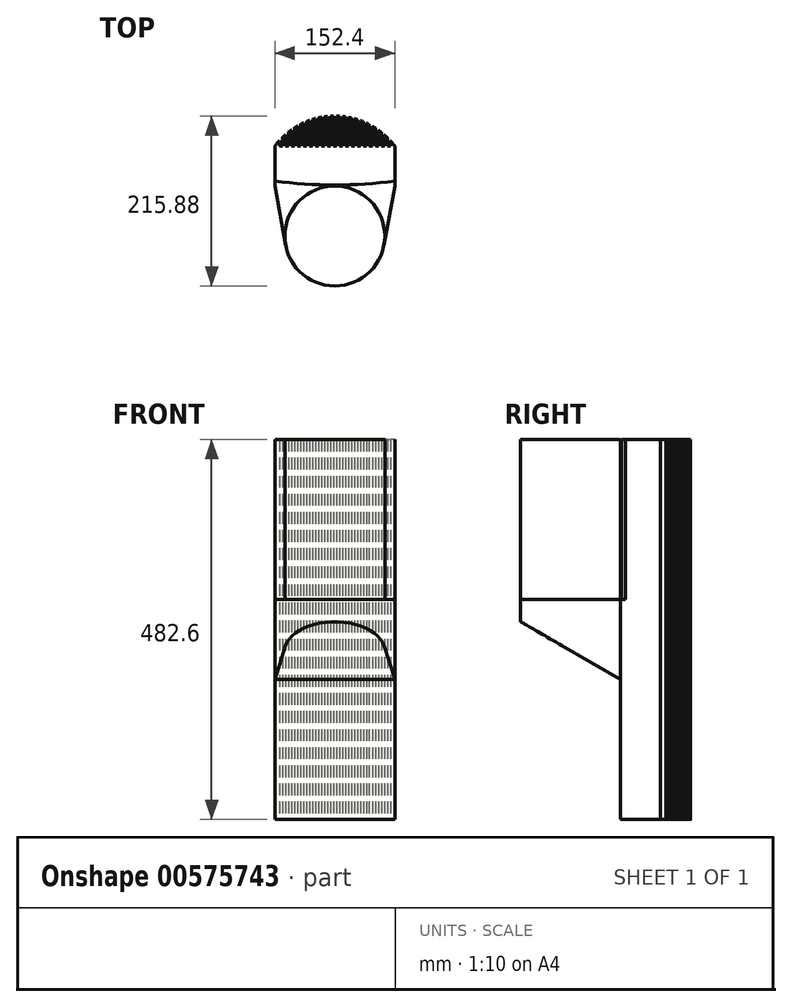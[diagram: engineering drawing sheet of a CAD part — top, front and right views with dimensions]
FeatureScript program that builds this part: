
annotation { "Feature Type Name" : "Feature", "Feature Type Description" : "" }
export const myFeature = defineFeature(function(context is Context, id is Id, definition is map)
    precondition{}
    {
        {
            var Q0;
            Q0=qCreatedBy(makeId("Top.planeOp"),FACE);
            var sketch = newSketch(context, id + "F0", { "sketchPlane" : qUnion([Q0])});
            skLineSegment(sketch, "E0", {"start": v(-76.2, 50.8) * mm, "end": v(-76.2, 0) * mm});
            skLineSegment(sketch, "E1", {"start": v(-76.2, 0) * mm, "end": v(76.2, 0) * mm});
            skLineSegment(sketch, "E2", {"start": v(76.2, 0) * mm, "end": v(76.2, 50.8) * mm});
            skArc(sketch, "E3", {"start": v(76.2, 50.8) * mm, "mid": v(0, 88.9) * mm, "end": v(-76.2, 50.8) * mm});
            skLineSegment(sketch, "E4", {"start": v(0, 88.9) * mm, "end": v(0, 0) * mm, "construction": true});
            skSolve(sketch);
        }
        {
            var Q0;
            Q0=makeQuery(id+"F0.imprint","IMPRINT",FACE,{"disambiguationData":[TD([[makeQuery(id+"F0.imprint","IMPRINT",EDGE,{"derivedFrom":sQuery(id+"F0.wireOp",EDGE,"E0")}),1.0]])]});
            extrude(context, id + "F1", {"entities" : qUnion([Q0]), "depth" : 482.6 * mm, "offsetDistance" : 25.4 * mm});
        }
        {
            var Q0;
            Q0=makeQuery(id+"F1.opExtrude","CAP_FACE",FACE,{"disambiguationData":[OSD([sQuery(id+"F0.wireOp",EDGE,"E0"),sQuery(id+"F0.wireOp",EDGE,"E1"),sQuery(id+"F0.wireOp",EDGE,"E2"),sQuery(id+"F0.wireOp",EDGE,"E3")])],"isStart":false});
            var sketch = newSketch(context, id + "F2", { "sketchPlane" : qUnion([Q0])});
            skLineSegment(sketch, "E5.bottom", {"start": v(-1.9, 88.9) * mm, "end": v(1.9, 88.9) * mm});
            skLineSegment(sketch, "E5.top", {"start": v(-1.9, 50.8) * mm, "end": v(1.9, 50.8) * mm});
            skLineSegment(sketch, "E5.left", {"start": v(-1.9, 88.9) * mm, "end": v(-1.9, 50.8) * mm});
            skLineSegment(sketch, "E5.right", {"start": v(1.9, 88.9) * mm, "end": v(1.9, 50.8) * mm});
            skLineSegment(sketch, "E6.1.0.0", {"start": v(9.52, 88.9) * mm, "end": v(9.52, 50.8) * mm});
            skLineSegment(sketch, "E6.1.0.1", {"start": v(5.71, 88.9) * mm, "end": v(5.71, 50.8) * mm});
            skLineSegment(sketch, "E6.1.0.2", {"start": v(5.71, 50.8) * mm, "end": v(9.52, 50.8) * mm});
            skLineSegment(sketch, "E6.1.0.3", {"start": v(5.71, 88.9) * mm, "end": v(9.52, 88.9) * mm});
            skLineSegment(sketch, "E6.2.0.0", {"start": v(17.14, 88.9) * mm, "end": v(17.14, 50.8) * mm});
            skLineSegment(sketch, "E6.2.0.1", {"start": v(13.33, 88.9) * mm, "end": v(13.33, 50.8) * mm});
            skLineSegment(sketch, "E6.2.0.2", {"start": v(13.33, 50.8) * mm, "end": v(17.14, 50.8) * mm});
            skLineSegment(sketch, "E6.2.0.3", {"start": v(13.33, 88.9) * mm, "end": v(17.14, 88.9) * mm});
            skLineSegment(sketch, "E6.3.0.0", {"start": v(24.76, 88.9) * mm, "end": v(24.76, 50.8) * mm});
            skLineSegment(sketch, "E6.3.0.1", {"start": v(20.95, 88.9) * mm, "end": v(20.95, 50.8) * mm});
            skLineSegment(sketch, "E6.3.0.2", {"start": v(20.95, 50.8) * mm, "end": v(24.76, 50.8) * mm});
            skLineSegment(sketch, "E6.3.0.3", {"start": v(20.95, 88.9) * mm, "end": v(24.76, 88.9) * mm});
            skLineSegment(sketch, "E6.4.0.0", {"start": v(32.38, 88.9) * mm, "end": v(32.38, 50.8) * mm});
            skLineSegment(sketch, "E6.4.0.1", {"start": v(28.57, 88.9) * mm, "end": v(28.57, 50.8) * mm});
            skLineSegment(sketch, "E6.4.0.2", {"start": v(28.57, 50.8) * mm, "end": v(32.38, 50.8) * mm});
            skLineSegment(sketch, "E6.4.0.3", {"start": v(28.57, 88.9) * mm, "end": v(32.38, 88.9) * mm});
            skLineSegment(sketch, "E6.5.0.0", {"start": v(40, 88.9) * mm, "end": v(40, 50.8) * mm});
            skLineSegment(sketch, "E6.5.0.1", {"start": v(36.2, 88.9) * mm, "end": v(36.2, 50.8) * mm});
            skLineSegment(sketch, "E6.5.0.2", {"start": v(36.2, 50.8) * mm, "end": v(40, 50.8) * mm});
            skLineSegment(sketch, "E6.5.0.3", {"start": v(36.2, 88.9) * mm, "end": v(40, 88.9) * mm});
            skLineSegment(sketch, "E6.6.0.0", {"start": v(47.62, 88.9) * mm, "end": v(47.62, 50.8) * mm});
            skLineSegment(sketch, "E6.6.0.1", {"start": v(43.81, 88.9) * mm, "end": v(43.81, 50.8) * mm});
            skLineSegment(sketch, "E6.6.0.2", {"start": v(43.81, 50.8) * mm, "end": v(47.62, 50.8) * mm});
            skLineSegment(sketch, "E6.6.0.3", {"start": v(43.81, 88.9) * mm, "end": v(47.62, 88.9) * mm});
            skLineSegment(sketch, "E6.7.0.0", {"start": v(55.24, 88.9) * mm, "end": v(55.24, 50.8) * mm});
            skLineSegment(sketch, "E6.7.0.1", {"start": v(51.43, 88.9) * mm, "end": v(51.43, 50.8) * mm});
            skLineSegment(sketch, "E6.7.0.2", {"start": v(51.43, 50.8) * mm, "end": v(55.24, 50.8) * mm});
            skLineSegment(sketch, "E6.7.0.3", {"start": v(51.43, 88.9) * mm, "end": v(55.24, 88.9) * mm});
            skLineSegment(sketch, "E6.8.0.0", {"start": v(62.86, 88.9) * mm, "end": v(62.86, 50.8) * mm});
            skLineSegment(sketch, "E6.8.0.1", {"start": v(59.05, 88.9) * mm, "end": v(59.05, 50.8) * mm});
            skLineSegment(sketch, "E6.8.0.2", {"start": v(59.05, 50.8) * mm, "end": v(62.86, 50.8) * mm});
            skLineSegment(sketch, "E6.8.0.3", {"start": v(59.05, 88.9) * mm, "end": v(62.86, 88.9) * mm});
            skLineSegment(sketch, "E6.9.0.0", {"start": v(70.48, 88.9) * mm, "end": v(70.48, 50.8) * mm});
            skLineSegment(sketch, "E6.9.0.1", {"start": v(66.67, 88.9) * mm, "end": v(66.67, 50.8) * mm});
            skLineSegment(sketch, "E6.9.0.2", {"start": v(66.67, 50.8) * mm, "end": v(70.48, 50.8) * mm});
            skLineSegment(sketch, "E6.9.0.3", {"start": v(66.67, 88.9) * mm, "end": v(70.48, 88.9) * mm});
            skLineSegment(sketch, "E6.direction1", {"start": v(-1.9, 50.8) * mm, "end": v(5.71, 50.8) * mm, "construction": true});
            skLineSegment(sketch, "E7.1.0.0", {"start": v(-5.72, 88.9) * mm, "end": v(-5.72, 50.8) * mm});
            skLineSegment(sketch, "E7.1.0.1", {"start": v(-9.53, 88.9) * mm, "end": v(-9.53, 50.8) * mm});
            skLineSegment(sketch, "E7.1.0.2", {"start": v(-9.53, 50.8) * mm, "end": v(-5.72, 50.8) * mm});
            skLineSegment(sketch, "E7.1.0.3", {"start": v(-9.53, 88.9) * mm, "end": v(-5.72, 88.9) * mm});
            skLineSegment(sketch, "E7.2.0.0", {"start": v(-13.34, 88.9) * mm, "end": v(-13.34, 50.8) * mm});
            skLineSegment(sketch, "E7.2.0.1", {"start": v(-17.15, 88.9) * mm, "end": v(-17.15, 50.8) * mm});
            skLineSegment(sketch, "E7.2.0.2", {"start": v(-17.15, 50.8) * mm, "end": v(-13.34, 50.8) * mm});
            skLineSegment(sketch, "E7.2.0.3", {"start": v(-17.15, 88.9) * mm, "end": v(-13.34, 88.9) * mm});
            skLineSegment(sketch, "E7.3.0.0", {"start": v(-20.96, 88.9) * mm, "end": v(-20.96, 50.8) * mm});
            skLineSegment(sketch, "E7.3.0.1", {"start": v(-24.77, 88.9) * mm, "end": v(-24.77, 50.8) * mm});
            skLineSegment(sketch, "E7.3.0.2", {"start": v(-24.77, 50.8) * mm, "end": v(-20.96, 50.8) * mm});
            skLineSegment(sketch, "E7.3.0.3", {"start": v(-24.77, 88.9) * mm, "end": v(-20.96, 88.9) * mm});
            skLineSegment(sketch, "E7.4.0.0", {"start": v(-28.58, 88.9) * mm, "end": v(-28.58, 50.8) * mm});
            skLineSegment(sketch, "E7.4.0.1", {"start": v(-32.39, 88.9) * mm, "end": v(-32.39, 50.8) * mm});
            skLineSegment(sketch, "E7.4.0.2", {"start": v(-32.39, 50.8) * mm, "end": v(-28.58, 50.8) * mm});
            skLineSegment(sketch, "E7.4.0.3", {"start": v(-32.39, 88.9) * mm, "end": v(-28.58, 88.9) * mm});
            skLineSegment(sketch, "E7.5.0.0", {"start": v(-36.2, 88.9) * mm, "end": v(-36.2, 50.8) * mm});
            skLineSegment(sketch, "E7.5.0.1", {"start": v(-40, 88.9) * mm, "end": v(-40, 50.8) * mm});
            skLineSegment(sketch, "E7.5.0.2", {"start": v(-40, 50.8) * mm, "end": v(-36.2, 50.8) * mm});
            skLineSegment(sketch, "E7.5.0.3", {"start": v(-40, 88.9) * mm, "end": v(-36.2, 88.9) * mm});
            skLineSegment(sketch, "E7.6.0.0", {"start": v(-43.82, 88.9) * mm, "end": v(-43.82, 50.8) * mm});
            skLineSegment(sketch, "E7.6.0.1", {"start": v(-47.63, 88.9) * mm, "end": v(-47.63, 50.8) * mm});
            skLineSegment(sketch, "E7.6.0.2", {"start": v(-47.63, 50.8) * mm, "end": v(-43.82, 50.8) * mm});
            skLineSegment(sketch, "E7.6.0.3", {"start": v(-47.63, 88.9) * mm, "end": v(-43.82, 88.9) * mm});
            skLineSegment(sketch, "E7.7.0.0", {"start": v(-51.44, 88.9) * mm, "end": v(-51.44, 50.8) * mm});
            skLineSegment(sketch, "E7.7.0.1", {"start": v(-55.25, 88.9) * mm, "end": v(-55.25, 50.8) * mm});
            skLineSegment(sketch, "E7.7.0.2", {"start": v(-55.25, 50.8) * mm, "end": v(-51.44, 50.8) * mm});
            skLineSegment(sketch, "E7.7.0.3", {"start": v(-55.25, 88.9) * mm, "end": v(-51.44, 88.9) * mm});
            skLineSegment(sketch, "E7.8.0.0", {"start": v(-59.06, 88.9) * mm, "end": v(-59.06, 50.8) * mm});
            skLineSegment(sketch, "E7.8.0.1", {"start": v(-62.87, 88.9) * mm, "end": v(-62.87, 50.8) * mm});
            skLineSegment(sketch, "E7.8.0.2", {"start": v(-62.87, 50.8) * mm, "end": v(-59.06, 50.8) * mm});
            skLineSegment(sketch, "E7.8.0.3", {"start": v(-62.87, 88.9) * mm, "end": v(-59.06, 88.9) * mm});
            skLineSegment(sketch, "E7.9.0.0", {"start": v(-66.68, 88.9) * mm, "end": v(-66.68, 50.8) * mm});
            skLineSegment(sketch, "E7.9.0.1", {"start": v(-70.49, 88.9) * mm, "end": v(-70.49, 50.8) * mm});
            skLineSegment(sketch, "E7.9.0.2", {"start": v(-70.49, 50.8) * mm, "end": v(-66.68, 50.8) * mm});
            skLineSegment(sketch, "E7.9.0.3", {"start": v(-70.49, 88.9) * mm, "end": v(-66.68, 88.9) * mm});
            skLineSegment(sketch, "E7.direction1", {"start": v(-1.9, 50.8) * mm, "end": v(-9.53, 50.8) * mm, "construction": true});
            skSolve(sketch);
        }
        {
            var Q0;
            Q0=qSketchRegion(id+"F2",true);
            extrude(context, id + "F3", {"entities" : qUnion([Q0]), "operationType" : NewBodyOperationType.REMOVE, "oppositeDirection" : true, "depth" : 482.6 * mm, "offsetDistance" : 25.4 * mm});
        }
        {
            var Q0;
            Q0=makeQuery(id+"F1.opExtrude","CAP_FACE",FACE,{"disambiguationData":[OSD([sQuery(id+"F0.wireOp",EDGE,"E0"),sQuery(id+"F0.wireOp",EDGE,"E1"),sQuery(id+"F0.wireOp",EDGE,"E2"),sQuery(id+"F0.wireOp",EDGE,"E3")])],"isStart":false});
            var sketch = newSketch(context, id + "F4", { "sketchPlane" : qUnion([Q0])});
            skCircle(sketch, "E8", {"center": v(0, -63.5) * mm, "radius": 63.5 * mm});
            skLineSegment(sketch, "E9", {"start": v(-76.2, 0) * mm, "end": v(-62.46, -74.95) * mm});
            skLineSegment(sketch, "E10", {"start": v(76.2, 0) * mm, "end": v(62.46, -74.95) * mm});
            skLineSegment(sketch, "E11", {"start": v(76.2, 0) * mm, "end": v(-76.2, 0) * mm});
            skSolve(sketch);
        }
        {
            var Q0;
            Q0=qSketchRegion(id+"F4",true);
            extrude(context, id + "F5", {"entities" : qUnion([Q0]), "operationType" : NewBodyOperationType.ADD, "oppositeDirection" : true, "depth" : 304.8 * mm, "offsetDistance" : 25.4 * mm});
        }
        {
            var Q0;
            Q0=makeQuery(id+"F1.opExtrude","SWEPT_FACE",FACE,{"disambiguationData":[OSD([sQuery(id+"F0.wireOp",EDGE,"E2")])]});
            var sketch = newSketch(context, id + "F6", { "sketchPlane" : qUnion([Q0])});
            skLineSegment(sketch, "E12", {"start": v(0, 177.8) * mm, "end": v(-138.08, 257.52) * mm});
            skLineSegment(sketch, "E13", {"start": v(-138.08, 257.52) * mm, "end": v(-138.08, 177.8) * mm});
            skLineSegment(sketch, "E14", {"start": v(-138.08, 177.8) * mm, "end": v(0, 177.8) * mm});
            skLineSegment(sketch, "E15.bottom", {"start": v(0, 482.6) * mm, "end": v(-138.08, 482.6) * mm});
            skLineSegment(sketch, "E15.top", {"start": v(0, 279.4) * mm, "end": v(-138.08, 279.4) * mm});
            skLineSegment(sketch, "E15.left", {"start": v(0, 482.6) * mm, "end": v(0, 279.4) * mm});
            skLineSegment(sketch, "E15.right", {"start": v(-138.08, 482.6) * mm, "end": v(-138.08, 279.4) * mm});
            skSolve(sketch);
        }
        {
            var Q0;
            Q0=qSketchRegion(id+"F6",true);
            extrude(context, id + "F7", {"entities" : qUnion([Q0]), "operationType" : NewBodyOperationType.REMOVE, "oppositeDirection" : true, "depth" : 254 * mm, "offsetDistance" : 25.4 * mm});
        }
        {
            var Q0;
            Q0=makeQuery(id+"F7.boolean.opBoolean","COPY",FACE,{"derivedFrom":makeQuery(id+"F7.opExtrude","SWEPT_FACE",FACE,{"disambiguationData":[OSD([sQuery(id+"F6.wireOp",EDGE,"E15.top")])]})});
            var sketch = newSketch(context, id + "F8", { "sketchPlane" : qUnion([Q0])});
            skCircle(sketch, "E16", {"center": v(0, -63.5) * mm, "radius": 63.5 * mm});
            skSolve(sketch);
        }
        {
            var Q0;
            Q0=qSketchRegion(id+"F8",true);
            var Q1;
            Q1=makeQuery(id+"F5.boolean.opBoolean","MERGE",FACE,{"derivedFrom":[makeQuery(id+"F1.opExtrude","CAP_FACE",FACE,{"disambiguationData":[OSD([sQuery(id+"F0.wireOp",EDGE,"E0"),sQuery(id+"F0.wireOp",EDGE,"E1"),sQuery(id+"F0.wireOp",EDGE,"E2"),sQuery(id+"F0.wireOp",EDGE,"E3")])],"isStart":false}),makeQuery(id+"F5.opExtrude","CAP_FACE",FACE,{"disambiguationData":[OSD([sQuery(id+"F4.wireOp",EDGE,"E8"),sQuery(id+"F4.wireOp",EDGE,"E9"),sQuery(id+"F4.wireOp",EDGE,"E10"),sQuery(id+"F4.wireOp",EDGE,"E11")])],"isStart":true})]});
            extrude(context, id + "F9", {"entities" : qUnion([Q0]), "endBound" : BoundingType.UP_TO_SURFACE, "depth" : 203.2 * mm, "endBoundEntityFace" : qUnion([Q1]), "offsetDistance" : 25.4 * mm});
        }
        {
            var Q0;
            Q0=makeQuery(id+"F5.boolean.opBoolean","MERGE",FACE,{"derivedFrom":[makeQuery(id+"F1.opExtrude","CAP_FACE",FACE,{"disambiguationData":[OSD([sQuery(id+"F0.wireOp",EDGE,"E0"),sQuery(id+"F0.wireOp",EDGE,"E1"),sQuery(id+"F0.wireOp",EDGE,"E2"),sQuery(id+"F0.wireOp",EDGE,"E3")])],"isStart":false}),makeQuery(id+"F5.opExtrude","CAP_FACE",FACE,{"disambiguationData":[OSD([sQuery(id+"F4.wireOp",EDGE,"E8"),sQuery(id+"F4.wireOp",EDGE,"E9"),sQuery(id+"F4.wireOp",EDGE,"E10"),sQuery(id+"F4.wireOp",EDGE,"E11")])],"isStart":true})]});
            var sketch = newSketch(context, id + "F10", { "sketchPlane" : qUnion([Q0])});
            skLineSegment(sketch, "E17", {"start": v(-76.2, 6.35) * mm, "end": v(76.2, 6.35) * mm, "construction": true});
            skArc(sketch, "E18", {"start": v(-76.2, 6.35) * mm, "mid": v(0, 1.27) * mm, "end": v(76.2, 6.35) * mm});
            skLineSegment(sketch, "E19", {"start": v(76.2, 6.35) * mm, "end": v(76.2, 0) * mm});
            skLineSegment(sketch, "E20", {"start": v(76.2, 0) * mm, "end": v(-76.2, 0) * mm});
            skLineSegment(sketch, "E21", {"start": v(-76.2, 0) * mm, "end": v(-76.2, 6.35) * mm});
            skSolve(sketch);
        }
        {
            var Q0;
            Q0 = qSketchRegion(id + "F10", true);
            var Q1;
            Q1=makeQuery(id+"F7.boolean.opBoolean","COPY",FACE,{"derivedFrom":makeQuery(id+"F7.opExtrude","SWEPT_FACE",FACE,{"disambiguationData":[OSD([sQuery(id+"F6.wireOp",EDGE,"E15.top")])]})});
            extrude(context, id + "F11", {"entities" : qUnion([Q0]), "operationType" : NewBodyOperationType.REMOVE, "endBound" : BoundingType.UP_TO_SURFACE, "oppositeDirection" : true, "depth" : 25.4 * mm, "endBoundEntityFace" : qUnion([Q1]), "offsetDistance" : 25.4 * mm});
        }
    });
